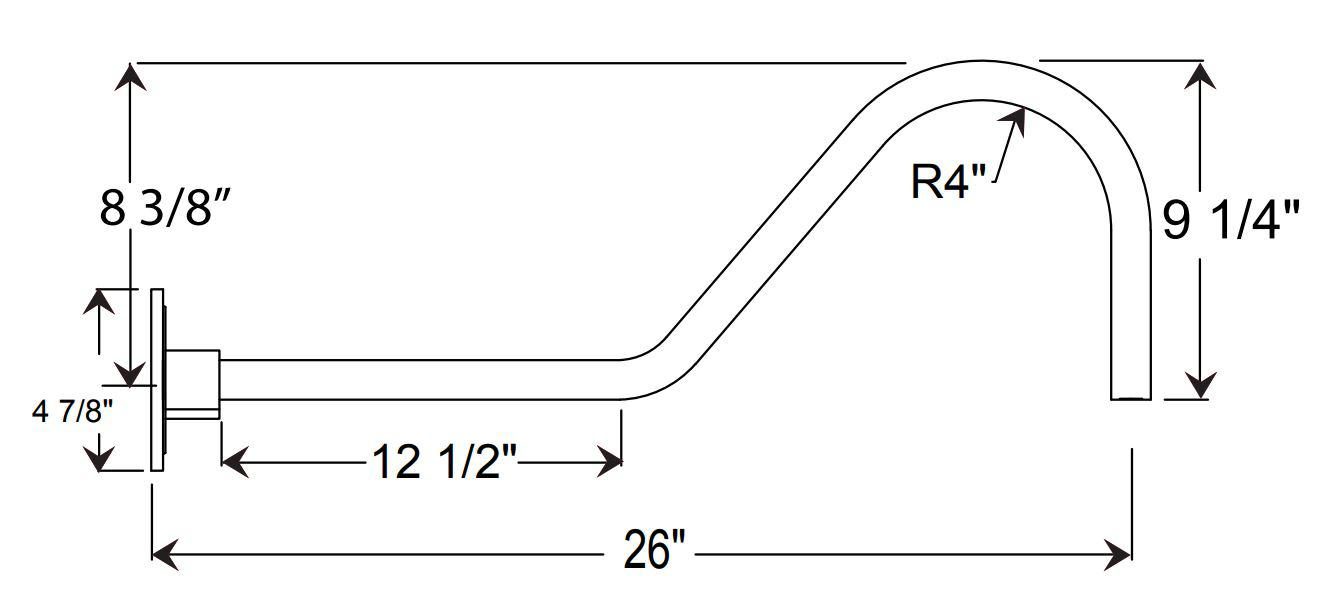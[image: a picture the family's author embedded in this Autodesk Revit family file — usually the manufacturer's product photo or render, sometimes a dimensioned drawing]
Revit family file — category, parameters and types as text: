
# Revit family: OSND LED 24,36,42
name_source: partatom
category: Lighting Fixtures
units: mm (PartAtom-declared; Revit-internal decimal feet)

## family parameters
Always vertical = Yes
Cut with Voids When Loaded = No
Light Source = Yes
OmniClass Number = 23.80.70.00
OmniClass Title = Lighting
Part Type = Normal
Room Calculation Point = No
Round Connector Dimension = Use Diameter
Shared = No
Work Plane-Based = No

## types (3) — shared parameters
Apparent Load = 24 VA
Body Colour = Spun aluminium
Body Material = body
Bulb = Bulb
CRI = >90
Canopy Body = body
Color Filter = 16777215
Construction Material = Heavy Duty spun aluminum.
Default Elevation = 0' - 0"
Description = 120-277 Voltage
Dimming = 1%
Dimming Lamp Color Temperature Shift = <None>
Efficiency = 65-125 lumens per watt
Lamp = LED
Life = L70 50,000 hours
Load Classification = Lighting
Manufacturer = ANP Lighting
Photometric Web File = generic
Power Factor = 1
Tilt Angle = 90.00°
URL = https://www.anplighting.com
Voltage = 277 V
Warranty = 5 year limited warranty
Wattage Comments = 24 W
b = 0' - 2"

## per-type parameters (varying)
| type | Fixture Diameter | Fixture Height | OSND24 | OSND36 | OSND42 | Weight | a |
| OSND24 | 2' - 0" | 1' - 8" | Yes | No | No | 16.0 lbs | 1' - 6" |
| OSND36 | 3' - 0" | 2' - 2" | No | Yes | No | 26.5 lbs | 1' - 6" |
| OSND42 | 3' - 6" | 2' - 5" | No | No | Yes | 34.5 lbs | 1' - 8" |

note: column(s) folded — value = type name in every type: Model

## geometry (parser evidence)
native form markers: Sweep x35
no freeform markers — native parametric forms only
